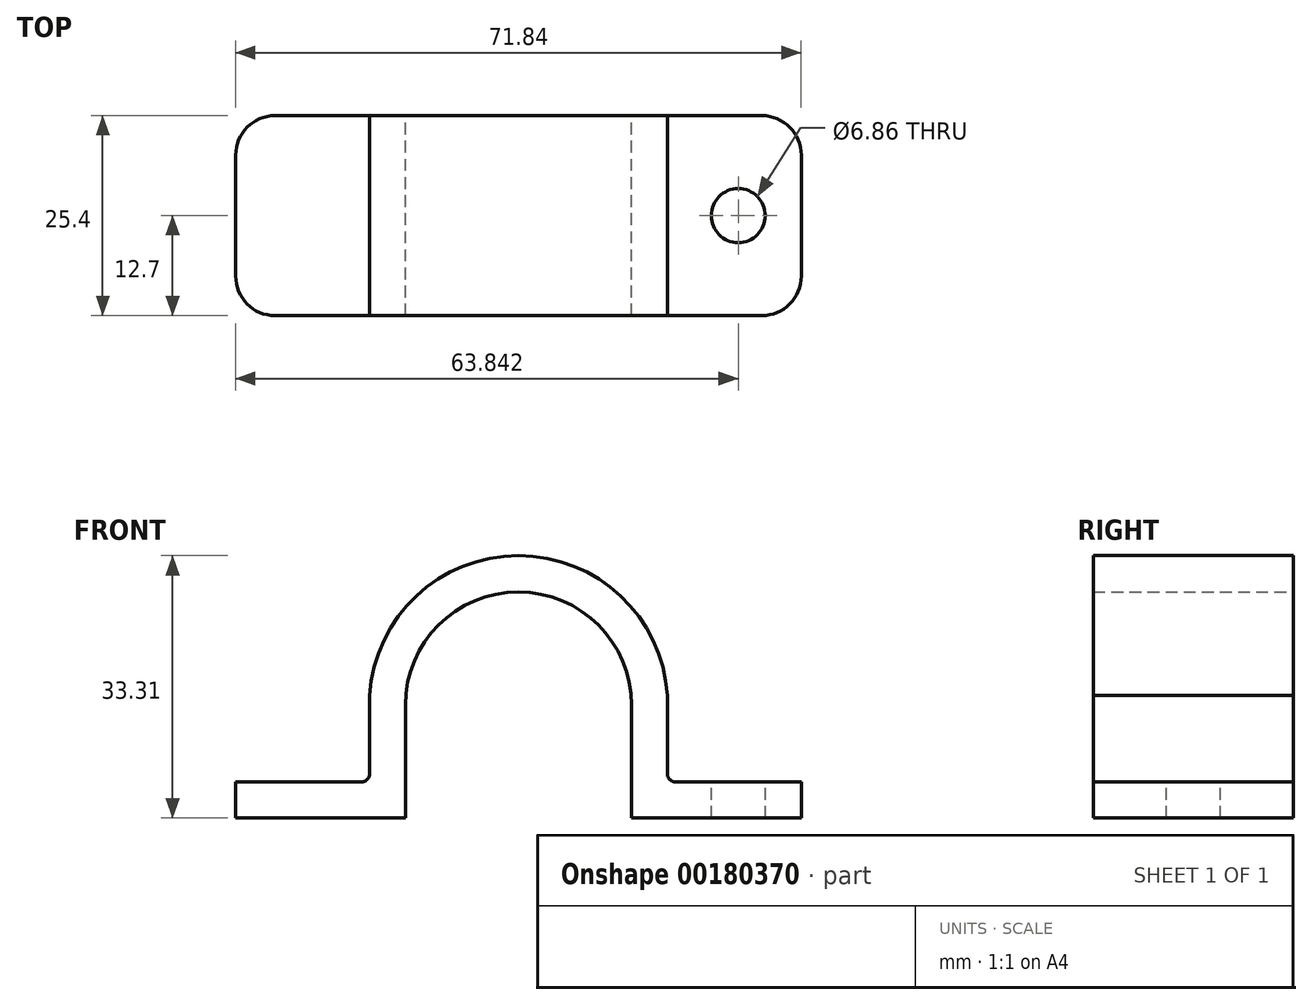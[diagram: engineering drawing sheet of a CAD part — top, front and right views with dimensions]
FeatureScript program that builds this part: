
annotation { "Feature Type Name" : "Feature", "Feature Type Description" : "" }
export const myFeature = defineFeature(function(context is Context, id is Id, definition is map)
    precondition{}
    {
        {
            assignVariable(context, id + "F0", {"name" : "CE_MCLAMP_WIDTH", "anyValue" : 25.4});
        }
        {
            var Q0;
            Q0=qCreatedBy(makeId("Front.planeOp"),FACE);
            var sketch = newSketch(context, id + "F1", { "sketchPlane" : qUnion([Q0])});
            skLineSegment(sketch, "E0", {"start": v(0, 0) * mm, "end": v(0, 14.35) * mm, "construction": true});
            skCircle(sketch, "E1", {"center": v(0, 14.35) * mm, "radius": 14.35 * mm, "construction": true});
            skLineSegment(sketch, "E2", {"start": v(14.35, 14.35) * mm, "end": v(14.35, 0) * mm});
            skLineSegment(sketch, "E3", {"start": v(14.35, 0) * mm, "end": v(35.92, 0) * mm});
            skLineSegment(sketch, "E4", {"start": v(35.92, 0) * mm, "end": v(35.92, 4.57) * mm});
            skLineSegment(sketch, "E5", {"start": v(35.92, 4.57) * mm, "end": v(18.92, 4.57) * mm});
            skLineSegment(sketch, "E6", {"start": v(18.92, 4.57) * mm, "end": v(18.92, 15.57) * mm});
            skArc(sketch, "E7", {"start": v(14.35, 14.35) * mm, "mid": v(10.15, 24.5) * mm, "end": v(0, 28.7) * mm});
            skArc(sketch, "E8", {"start": v(18.92, 15.57) * mm, "mid": v(12.97, 28.18) * mm, "end": v(0, 33.31) * mm});
            skLineSegment(sketch, "E9.MirrorCS", {"start": v(-35.92, 0) * mm, "end": v(-35.92, 4.57) * mm});
            skLineSegment(sketch, "E10.MirrorCS", {"start": v(-35.92, 4.57) * mm, "end": v(-18.92, 4.57) * mm});
            skLineSegment(sketch, "E11.MirrorCS", {"start": v(-18.92, 4.57) * mm, "end": v(-18.92, 15.57) * mm});
            skLineSegment(sketch, "E12.MirrorCS", {"start": v(-14.35, 14.35) * mm, "end": v(-14.35, 0) * mm});
            skLineSegment(sketch, "E13.MirrorCS", {"start": v(-14.35, 0) * mm, "end": v(-35.92, 0) * mm});
            skArc(sketch, "E14.MirrorCS", {"start": v(-18.92, 15.57) * mm, "mid": v(-12.97, 28.18) * mm, "end": v(0, 33.31) * mm});
            skArc(sketch, "E15.MirrorCS", {"start": v(-14.35, 14.35) * mm, "mid": v(-10.15, 24.5) * mm, "end": v(0, 28.7) * mm});
            skSolve(sketch);
        }
        {
            var Q0;
            Q0 = qSketchRegion(id + "F1", true);
            extrude(context, id + "F2", {"entities" : qUnion([Q0]), "depth" : (getVariable(context, 'CE_MCLAMP_WIDTH')) * mm});
        }
        {
            var Q0;
            Q0=makeQuery(id+"F2.opExtrude","SWEPT_EDGE",EDGE,{"disambiguationData":[OSD([sQuery(id+"F1.wireOp",EDGE,"E10.MirrorCS"),sQuery(id+"F1.wireOp",EDGE,"E11.MirrorCS")])]});
            var Q1;
            Q1=makeQuery(id+"F2.opExtrude","SWEPT_EDGE",EDGE,{"disambiguationData":[OSD([sQuery(id+"F1.wireOp",EDGE,"E5"),sQuery(id+"F1.wireOp",EDGE,"E6")])]});
            fillet(context, id + "F3", {"entities" : qUnion([Q0, Q1]), "radius" : 1 * mm, "tangentPropagation" : true, "allowEdgeOverflow" : false});
        }
        {
            var Q0;
            Q0=makeQuery(id+"F2.opExtrude","CAP_EDGE",EDGE,{"disambiguationData":[OSD([sQuery(id+"F1.wireOp",EDGE,"E9.MirrorCS")])],"isStart":false});
            var Q1;
            Q1=makeQuery(id+"F2.opExtrude","CAP_EDGE",EDGE,{"disambiguationData":[OSD([sQuery(id+"F1.wireOp",EDGE,"E4")])],"isStart":false});
            var Q2;
            Q2=makeQuery(id+"F2.opExtrude","CAP_EDGE",EDGE,{"disambiguationData":[OSD([sQuery(id+"F1.wireOp",EDGE,"E4")])],"isStart":true});
            var Q3;
            Q3=makeQuery(id+"F2.opExtrude","CAP_EDGE",EDGE,{"disambiguationData":[OSD([sQuery(id+"F1.wireOp",EDGE,"E9.MirrorCS")])],"isStart":true});
            fillet(context, id + "F4", {"entities" : qUnion([Q0, Q1, Q2, Q3]), "radius" : 5 * mm, "tangentPropagation" : true, "allowEdgeOverflow" : false});
        }
        {
            var Q0;
            Q0=makeQuery(id+"F2.opExtrude","SWEPT_FACE",FACE,{"disambiguationData":[OSD([sQuery(id+"F1.wireOp",EDGE,"E5")])]});
            var sketch = newSketch(context, id + "F5", { "sketchPlane" : qUnion([Q0])});
            skLineSegment(sketch, "E16", {"start": v(35.92, -12.7) * mm, "end": v(19.92, -12.7) * mm, "construction": true});
            skCircle(sketch, "E17", {"center": v(27.92, -12.7) * mm, "radius": 3.43 * mm});
            skLineSegment(sketch, "E18", {"start": v(0, 0) * mm, "end": v(0, -25.4) * mm, "construction": true});
            skCircle(sketch, "E19.MirrorC", {"center": v(-27.92, -12.7) * mm, "radius": 3.43 * mm});
            skSolve(sketch);
        }
        {
            var Q0;
            Q0=makeQuery(id+"F5.imprint","IMPRINT",FACE,{"disambiguationData":[TD([[makeQuery(id+"F5.imprint","IMPRINT",EDGE,{"derivedFrom":sQuery(id+"F5.wireOp",EDGE,"E19.MirrorC")}),-1.0]])]});
            var Q1;
            Q1=makeQuery(id+"F5.imprint","IMPRINT",FACE,{"disambiguationData":[TD([[makeQuery(id+"F5.imprint","IMPRINT",EDGE,{"derivedFrom":sQuery(id+"F5.wireOp",EDGE,"E17")}),1.0]])]});
            var Q2;
            Q2=sQuery(id+"F5.wireOp",EDGE,"E17");
            var Q3;
            Q3=sQuery(id+"F5.wireOp",EDGE,"E19.MirrorC");
            extrude(context, id + "F6", {"entities" : qUnion([Q0, Q1]), "operationType" : NewBodyOperationType.REMOVE, "surfaceEntities" : qUnion([Q2, Q3]), "endBound" : BoundingType.THROUGH_ALL, "oppositeDirection" : true, "depth" : 25 * mm});
        }
    });
